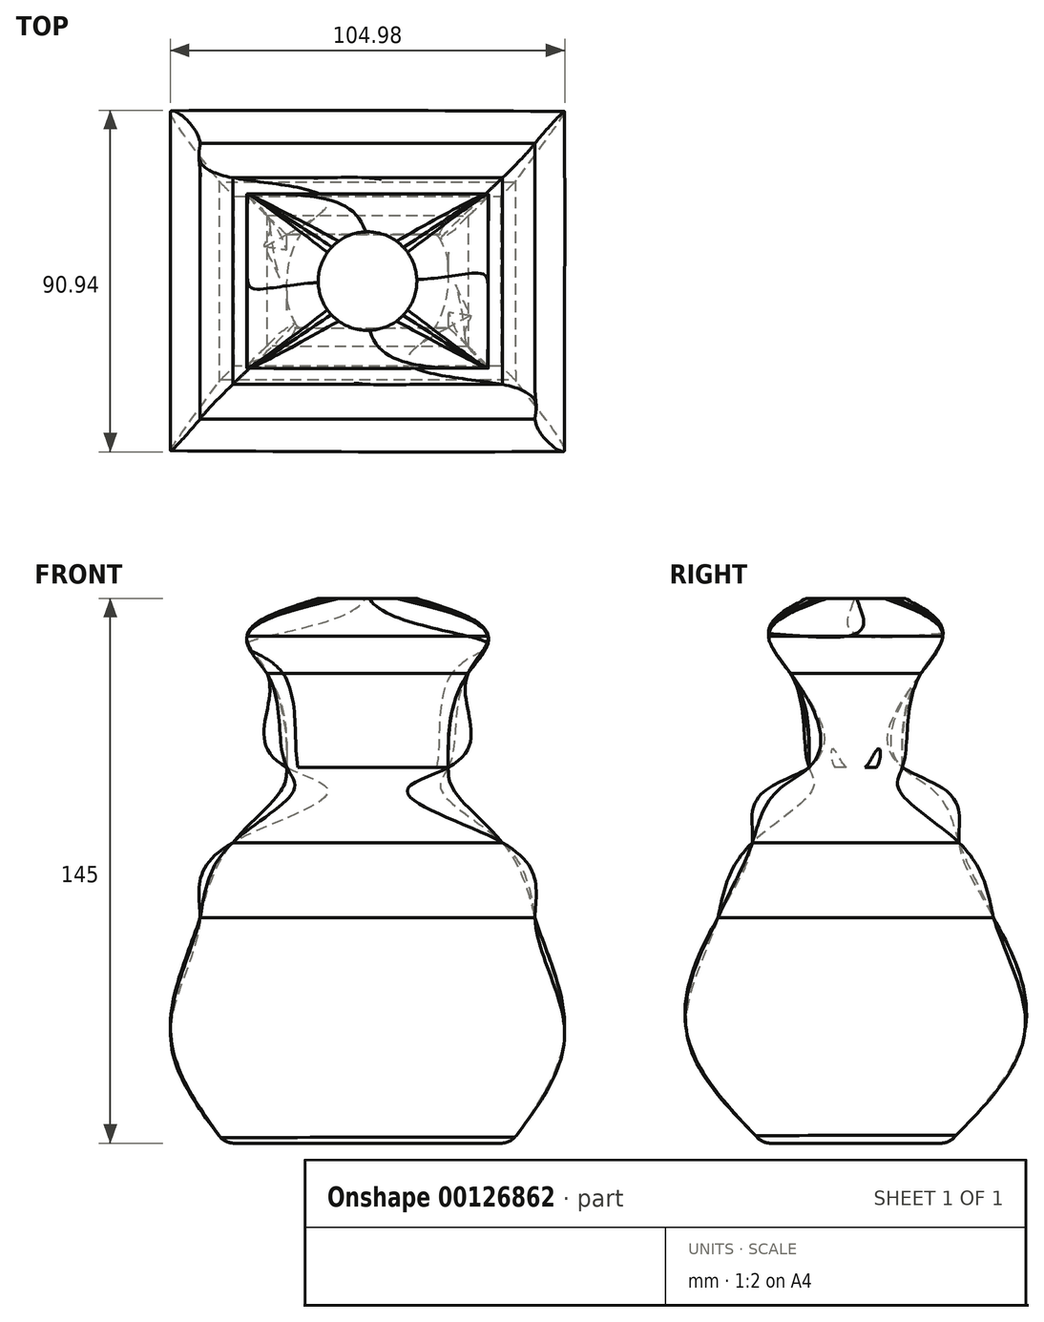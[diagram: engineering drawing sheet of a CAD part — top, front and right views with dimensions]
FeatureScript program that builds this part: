
annotation { "Feature Type Name" : "Feature", "Feature Type Description" : "" }
export const myFeature = defineFeature(function(context is Context, id is Id, definition is map)
    precondition{}
    {
        {
            var Q0;
            Q0=qCreatedBy(makeId("Top.planeOp"),FACE);
            var sketch = newSketch(context, id + "F0", { "sketchPlane" : qUnion([Q0])});
            skLineSegment(sketch, "E0.bottom", {"start": v(-21.47, 12.42) * mm, "end": v(21.47, 12.42) * mm});
            skLineSegment(sketch, "E0.top", {"start": v(-21.47, -12.42) * mm, "end": v(21.47, -12.42) * mm});
            skLineSegment(sketch, "E0.left", {"start": v(-21.47, 12.42) * mm, "end": v(-21.47, -12.42) * mm});
            skLineSegment(sketch, "E0.right", {"start": v(21.47, 12.42) * mm, "end": v(21.47, -12.42) * mm});
            skPoint(sketch, "E0.middle", {"position": v(0, 0) * mm});
            skSolve(sketch);
        }
        {
            var Q0;
            Q0=qCreatedBy(makeId("Top.planeOp"),FACE);
            cPlane(context, id + "F1", {"entities" : qUnion([Q0]), "cplaneType" : CPlaneType.OFFSET, "offset" : 25 * mm, "width" : 150 * mm, "height" : 150 * mm});
        }
        {
            var Q0;
            Q0=qCreatedBy(id+"F1.planeOp",FACE);
            cPlane(context, id + "F2", {"entities" : qUnion([Q0]), "cplaneType" : CPlaneType.OFFSET, "offset" : 10 * mm, "width" : 150 * mm, "height" : 150 * mm});
        }
        {
            var Q0;
            Q0=qCreatedBy(id+"F2.planeOp",FACE);
            cPlane(context, id + "F3", {"entities" : qUnion([Q0]), "cplaneType" : CPlaneType.OFFSET, "offset" : 10 * mm, "width" : 150 * mm, "height" : 150 * mm});
        }
        {
            var Q0;
            Q0=qCreatedBy(id+"F1.planeOp",FACE);
            var sketch = newSketch(context, id + "F4", { "sketchPlane" : qUnion([Q0])});
            skLineSegment(sketch, "E1.bottom", {"start": v(-26.74, 17.32) * mm, "end": v(26.74, 17.32) * mm});
            skLineSegment(sketch, "E1.top", {"start": v(-26.74, -17.32) * mm, "end": v(26.74, -17.32) * mm});
            skLineSegment(sketch, "E1.left", {"start": v(-26.74, 17.32) * mm, "end": v(-26.74, -17.32) * mm});
            skLineSegment(sketch, "E1.right", {"start": v(26.74, 17.32) * mm, "end": v(26.74, -17.32) * mm});
            skPoint(sketch, "E1.middle", {"position": v(0, 0) * mm});
            skSolve(sketch);
        }
        {
            var Q0;
            Q0=qCreatedBy(id+"F2.planeOp",FACE);
            var sketch = newSketch(context, id + "F5", { "sketchPlane" : qUnion([Q0])});
            skLineSegment(sketch, "E2.bottom", {"start": v(-32.09, -23.17) * mm, "end": v(32.09, -23.17) * mm});
            skLineSegment(sketch, "E2.top", {"start": v(-32.09, 23.17) * mm, "end": v(32.09, 23.17) * mm});
            skLineSegment(sketch, "E2.left", {"start": v(-32.09, -23.17) * mm, "end": v(-32.09, 23.17) * mm});
            skLineSegment(sketch, "E2.right", {"start": v(32.09, -23.17) * mm, "end": v(32.09, 23.17) * mm});
            skPoint(sketch, "E2.middle", {"position": v(0, 0) * mm});
            skSolve(sketch);
        }
        {
            var Q0;
            Q0=qCreatedBy(id+"F3.planeOp",FACE);
            var sketch = newSketch(context, id + "F6", { "sketchPlane" : qUnion([Q0])});
            skCircle(sketch, "E3", {"center": v(0, 0) * mm, "radius": 13.12 * mm});
            skSolve(sketch);
        }
        {
            var Q0;
            Q0 = qSketchRegion(id + "F0", true);
            var Q1;
            Q1 = qSketchRegion(id + "F4", true);
            var Q2;
            Q2 = qSketchRegion(id + "F5", true);
            var Q3;
            Q3 = qSketchRegion(id + "F6", true);
            loft(context, id + "F7", {"sheetProfilesArray" : [{ "sheetProfileEntities" : qUnion([Q0]) }, { "sheetProfileEntities" : qUnion([Q1]) }, { "sheetProfileEntities" : qUnion([Q2]) }, { "sheetProfileEntities" : qUnion([Q3]) }]});
        }
        {
            var Q0;
            Q0=qCreatedBy(makeId("Top.planeOp"),FACE);
            cPlane(context, id + "F8", {"entities" : qUnion([Q0]), "cplaneType" : CPlaneType.OFFSET, "offset" : 5 * mm, "oppositeDirection" : true, "width" : 150 * mm, "height" : 150 * mm});
        }
        {
            var Q0;
            Q0=qCreatedBy(id+"F8.planeOp",FACE);
            var sketch = newSketch(context, id + "F9", { "sketchPlane" : qUnion([Q0])});
            skCircle(sketch, "E4", {"center": v(0, 0) * mm, "radius": 22.37 * mm});
            skSolve(sketch);
        }
        {
            var Q0;
            Q0=qCreatedBy(id+"F8.planeOp",FACE);
            cPlane(context, id + "F10", {"entities" : qUnion([Q0]), "cplaneType" : CPlaneType.OFFSET, "offset" : 15 * mm, "oppositeDirection" : true, "width" : 150 * mm, "height" : 150 * mm});
        }
        {
            var Q0;
            Q0=qCreatedBy(id+"F10.planeOp",FACE);
            var sketch = newSketch(context, id + "F11", { "sketchPlane" : qUnion([Q0])});
            skLineSegment(sketch, "E5.bottom", {"start": v(35.9, -27.5) * mm, "end": v(-35.9, -27.5) * mm});
            skLineSegment(sketch, "E5.top", {"start": v(35.9, 27.5) * mm, "end": v(-35.9, 27.5) * mm});
            skLineSegment(sketch, "E5.left", {"start": v(35.9, -27.5) * mm, "end": v(35.9, 27.5) * mm});
            skLineSegment(sketch, "E5.right", {"start": v(-35.9, -27.5) * mm, "end": v(-35.9, 27.5) * mm});
            skPoint(sketch, "E5.middle", {"position": v(0, 0) * mm});
            skSolve(sketch);
        }
        {
            var Q0;
            Q0=qCreatedBy(id+"F10.planeOp",FACE);
            cPlane(context, id + "F12", {"entities" : qUnion([Q0]), "cplaneType" : CPlaneType.OFFSET, "offset" : 20 * mm, "oppositeDirection" : true, "width" : 150 * mm, "height" : 150 * mm});
        }
        {
            var Q0;
            Q0=qCreatedBy(id+"F12.planeOp",FACE);
            var sketch = newSketch(context, id + "F13", { "sketchPlane" : qUnion([Q0])});
            skLineSegment(sketch, "E6.bottom", {"start": v(44.56, 36.67) * mm, "end": v(-44.56, 36.67) * mm});
            skLineSegment(sketch, "E6.top", {"start": v(44.56, -36.67) * mm, "end": v(-44.56, -36.67) * mm});
            skLineSegment(sketch, "E6.left", {"start": v(44.56, 36.67) * mm, "end": v(44.56, -36.67) * mm});
            skLineSegment(sketch, "E6.right", {"start": v(-44.56, 36.67) * mm, "end": v(-44.56, -36.67) * mm});
            skPoint(sketch, "E6.middle", {"position": v(0, 0) * mm});
            skSolve(sketch);
        }
        {
            var Q0;
            Q0=qCreatedBy(id+"F12.planeOp",FACE);
            cPlane(context, id + "F14", {"entities" : qUnion([Q0]), "cplaneType" : CPlaneType.OFFSET, "offset" : 30 * mm, "oppositeDirection" : true, "width" : 150 * mm, "height" : 150 * mm});
        }
        {
            var Q0;
            Q0=qCreatedBy(id+"F14.planeOp",FACE);
            var sketch = newSketch(context, id + "F15", { "sketchPlane" : qUnion([Q0])});
            skLineSegment(sketch, "E7.bottom", {"start": v(52.46, -45.07) * mm, "end": v(-52.46, -45.07) * mm});
            skLineSegment(sketch, "E7.top", {"start": v(52.46, 45.07) * mm, "end": v(-52.46, 45.07) * mm});
            skLineSegment(sketch, "E7.left", {"start": v(52.46, -45.07) * mm, "end": v(52.46, 45.07) * mm});
            skLineSegment(sketch, "E7.right", {"start": v(-52.46, -45.07) * mm, "end": v(-52.46, 45.07) * mm});
            skPoint(sketch, "E7.middle", {"position": v(0, 0) * mm});
            skSolve(sketch);
        }
        {
            var Q0;
            Q0=qCreatedBy(id+"F14.planeOp",FACE);
            cPlane(context, id + "F16", {"entities" : qUnion([Q0]), "cplaneType" : CPlaneType.OFFSET, "offset" : 30 * mm, "oppositeDirection" : true, "width" : 150 * mm, "height" : 150 * mm});
        }
        {
            var Q0;
            Q0=qCreatedBy(id+"F16.planeOp",FACE);
            var sketch = newSketch(context, id + "F17", { "sketchPlane" : qUnion([Q0])});
            skLineSegment(sketch, "E8.bottom", {"start": v(38.02, -24.73) * mm, "end": v(-38.02, -24.73) * mm});
            skLineSegment(sketch, "E8.top", {"start": v(38.02, 24.73) * mm, "end": v(-38.02, 24.73) * mm});
            skLineSegment(sketch, "E8.left", {"start": v(38.02, -24.73) * mm, "end": v(38.02, 24.73) * mm});
            skLineSegment(sketch, "E8.right", {"start": v(-38.02, -24.73) * mm, "end": v(-38.02, 24.73) * mm});
            skPoint(sketch, "E8.middle", {"position": v(0, 0) * mm});
            skSolve(sketch);
        }
        {
            var Q1;
            Q1 = qSketchRegion(id + "F6", true);
            var Q2;
            Q2 = qSketchRegion(id + "F5", true);
            var Q3;
            Q3 = qSketchRegion(id + "F4", true);
            var Q4;
            Q4 = qSketchRegion(id + "F0", true);
            var Q5;
            Q5 = qSketchRegion(id + "F9", true);
            var Q6;
            Q6 = qSketchRegion(id + "F11", true);
            var Q7;
            Q7 = qSketchRegion(id + "F13", true);
            var Q8;
            Q8 = qSketchRegion(id + "F15", true);
            loft(context, id + "F18", {"operationType" : NewBodyOperationType.ADD, "sheetProfilesArray" : [{ "sheetProfileEntities" : qUnion([Q1]) }, { "sheetProfileEntities" : qUnion([Q2]) }, { "sheetProfileEntities" : qUnion([Q3]) }, { "sheetProfileEntities" : qUnion([Q4]) }, { "sheetProfileEntities" : qUnion([Q5]) }, { "sheetProfileEntities" : qUnion([Q6]) }, { "sheetProfileEntities" : qUnion([Q7]) }, { "sheetProfileEntities" : qUnion([Q8]) }]});
        }
        {
            var Q1;
            Q1 = qSketchRegion(id + "F6", true);
            var Q2;
            Q2 = qSketchRegion(id + "F5", true);
            var Q3;
            Q3 = qSketchRegion(id + "F4", true);
            var Q4;
            Q4 = qSketchRegion(id + "F0", true);
            var Q5;
            Q5 = qSketchRegion(id + "F9", true);
            var Q6;
            Q6 = qSketchRegion(id + "F11", true);
            var Q7;
            Q7 = qSketchRegion(id + "F13", true);
            var Q8;
            Q8 = qSketchRegion(id + "F15", true);
            var Q9;
            Q9 = qSketchRegion(id + "F17", true);
            loft(context, id + "F19", {"operationType" : NewBodyOperationType.ADD, "sheetProfilesArray" : [{ "sheetProfileEntities" : qUnion([Q1]) }, { "sheetProfileEntities" : qUnion([Q2]) }, { "sheetProfileEntities" : qUnion([Q3]) }, { "sheetProfileEntities" : qUnion([Q4]) }, { "sheetProfileEntities" : qUnion([Q5]) }, { "sheetProfileEntities" : qUnion([Q6]) }, { "sheetProfileEntities" : qUnion([Q7]) }, { "sheetProfileEntities" : qUnion([Q8]) }, { "sheetProfileEntities" : qUnion([Q9]) }]});
        }
        {
            var Q0;
            Q0=makeQuery(id+"F19.opLoft","CAP_FACE",FACE,{"disambiguationData":[OSD([makeQuery(id+"F17.imprint","IMPRINT",FACE,{"disambiguationData":[TD([[makeQuery(id+"F17.imprint","IMPRINT",EDGE,{"derivedFrom":sQuery(id+"F17.wireOp",EDGE,"E8.bottom")}),-1.0]])]})])],"isStart":true});
            fillet(context, id + "F20", {"entities" : qUnion([Q0]), "radius" : 5 * mm, "tangentPropagation" : true, "allowEdgeOverflow" : false});
        }
    });
